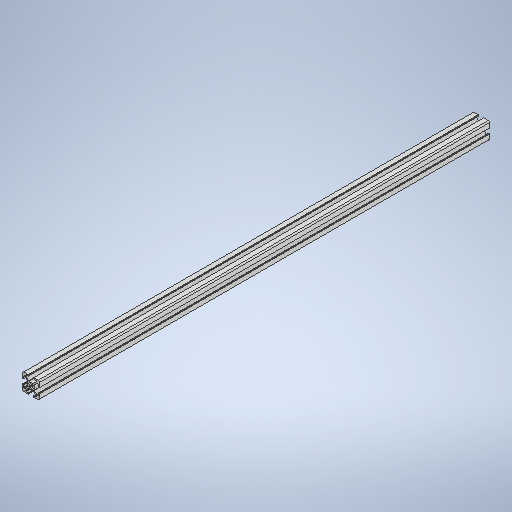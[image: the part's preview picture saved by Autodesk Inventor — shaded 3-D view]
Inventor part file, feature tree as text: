
AUTODESK INVENTOR PART (.ipt)
format: ipt  version: 2025 (Build 290162000, 162)  size: 368,128 bytes
history: native  units: mm
features: extrude x1, sketch x1
ambient origin geometry x8: Origin, YZ Plane, XZ Plane, XY Plane, X Axis, Y Axis, Z Axis, Center Point
bodies: Solid1 (feature_tree)
feature tree (2):
  extrude  "Extrusion1"  Depth=530.0mm
  sketch  "Sketch1"  dims[d0=530.0mm d1=0.0mm d2=1.0mm d3=1.0mm d4=1.0mm d5=0.15mm d6=0.25mm d7=0.375mm d8=14.3117mm d9=0.75mm d10=20.594885mm d11=0.0625mm d12=0.75mm d13=0.375mm]
